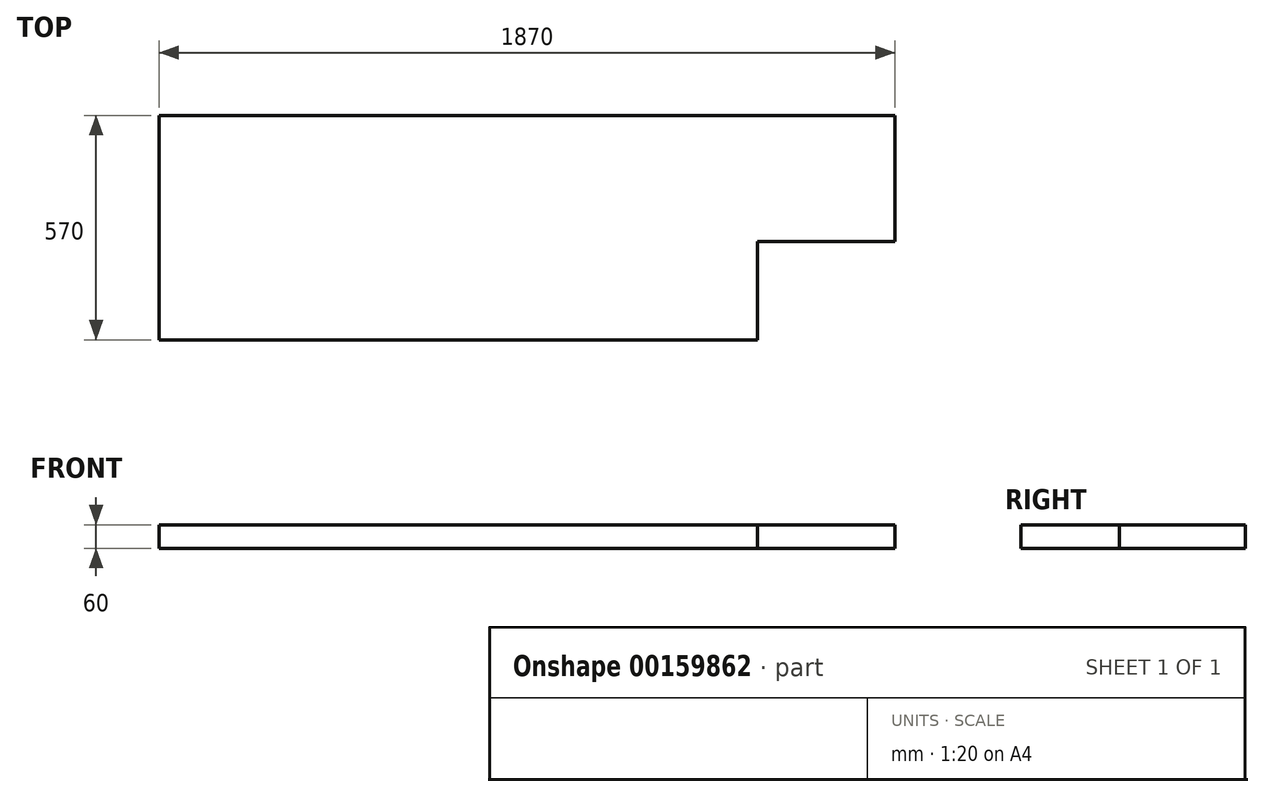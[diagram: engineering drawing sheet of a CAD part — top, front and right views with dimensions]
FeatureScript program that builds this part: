
annotation { "Feature Type Name" : "Feature", "Feature Type Description" : "" }
export const myFeature = defineFeature(function(context is Context, id is Id, definition is map)
    precondition{}
    {
        {
            assignVariable(context, id + "F0", {"name" : "t", "anyValue" : 60 * mm});
        }
        {
            var Q0;
            Q0=qCreatedBy(makeId("Top.planeOp"),FACE);
            var sketch = newSketch(context, id + "F1", { "sketchPlane" : qUnion([Q0])});
            skLineSegment(sketch, "E0.bottom", {"start": v(935, -285) * mm, "end": v(-935, -285) * mm});
            skLineSegment(sketch, "E0.top", {"start": v(935, 285) * mm, "end": v(-935, 285) * mm});
            skLineSegment(sketch, "E0.left", {"start": v(935, -285) * mm, "end": v(935, 285) * mm});
            skLineSegment(sketch, "E0.right", {"start": v(-935, -285) * mm, "end": v(-935, 285) * mm});
            skPoint(sketch, "E0.middle", {"position": v(0, 0) * mm});
            skLineSegment(sketch, "E1", {"start": v(585, -285) * mm, "end": v(585, -35) * mm});
            skLineSegment(sketch, "E2", {"start": v(585, -35) * mm, "end": v(935, -35) * mm});
            skSolve(sketch);
        }
        {
            var Q0;
            {var subQ2=sQuery(id+"F1.wireOp",EDGE,"E0.top");Q0=makeQuery(id+"F1.imprint","IMPRINT",FACE,{"disambiguationData":[TD([[makeQuery(id+"F1.imprint","IMPRINT",EDGE,{"derivedFrom":subQ2}),1.0]])]});}
            extrude(context, id + "F2", {"entities" : qUnion([Q0]), "depth" : getVariable(context, 't')});
        }
    });
